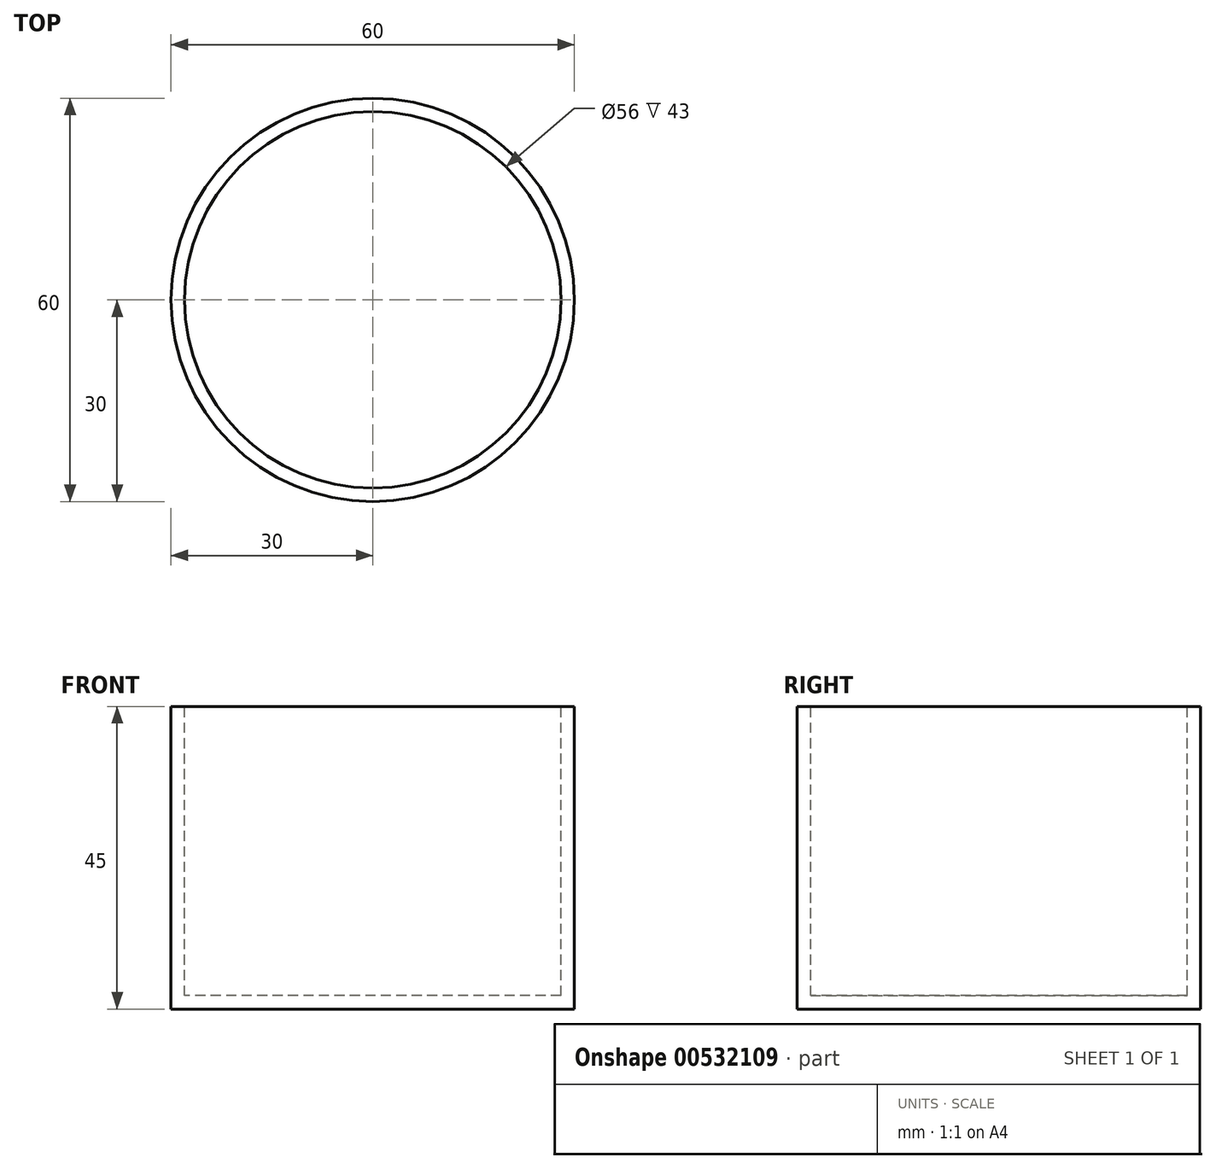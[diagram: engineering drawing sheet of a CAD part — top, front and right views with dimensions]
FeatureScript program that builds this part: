
annotation { "Feature Type Name" : "Feature", "Feature Type Description" : "" }
export const myFeature = defineFeature(function(context is Context, id is Id, definition is map)
    precondition{}
    {
        {
            var Q0;
            Q0=qCreatedBy(makeId("Top.planeOp"),FACE);
            var sketch = newSketch(context, id + "F0", { "sketchPlane" : qUnion([Q0])});
            skCircle(sketch, "E0", {"center": v(0, 0) * mm, "radius": 28 * mm});
            skCircle(sketch, "E1", {"center": v(0, 0) * mm, "radius": 30 * mm});
            skPoint(sketch, "E2", {"position": v(-28, 0) * mm});
            skPoint(sketch, "E3", {"position": v(0, 28) * mm});
            skPoint(sketch, "E4", {"position": v(28, 0) * mm});
            skPoint(sketch, "E5", {"position": v(0, -28) * mm});
            skPoint(sketch, "E6", {"position": v(30, 0) * mm});
            skPoint(sketch, "E7", {"position": v(0, 30) * mm});
            skPoint(sketch, "E8", {"position": v(-30, 0.03) * mm});
            skPoint(sketch, "E9", {"position": v(0, -30) * mm});
            skSolve(sketch);
        }
        {
            var Q0;
            Q0=makeQuery(id+"F0.imprint","IMPRINT",FACE,{"disambiguationData":[TD([[makeQuery(id+"F0.imprint","IMPRINT",EDGE,{"derivedFrom":sQuery(id+"F0.wireOp",EDGE,"E0")}),-1.0]])]});
            var Q1;
            Q1=makeQuery(id+"F0.imprint","IMPRINT",FACE,{"disambiguationData":[TD([[makeQuery(id+"F0.imprint","IMPRINT",EDGE,{"derivedFrom":sQuery(id+"F0.wireOp",EDGE,"E0")}),1.0]])]});
            var Q2;
            Q2=sQuery(id+"F0.wireOp",EDGE,"E1");
            extrude(context, id + "F1", {"entities" : qUnion([Q0, Q1]), "surfaceEntities" : qUnion([Q2]), "oppositeDirection" : true, "depth" : 45 * mm, "offsetDistance" : 25.4 * mm});
        }
        {
            var Q0;
            Q0=makeQuery(id+"F0.imprint","IMPRINT",FACE,{"disambiguationData":[TD([[makeQuery(id+"F0.imprint","IMPRINT",EDGE,{"derivedFrom":sQuery(id+"F0.wireOp",EDGE,"E0")}),1.0]])]});
            var Q1;
            Q1=sQuery(id+"F0.wireOp",EDGE,"E0");
            extrude(context, id + "F2", {"entities" : qUnion([Q0]), "operationType" : NewBodyOperationType.REMOVE, "surfaceEntities" : qUnion([Q1]), "oppositeDirection" : true, "depth" : 43 * mm, "offsetDistance" : 25.4 * mm});
        }
    });
